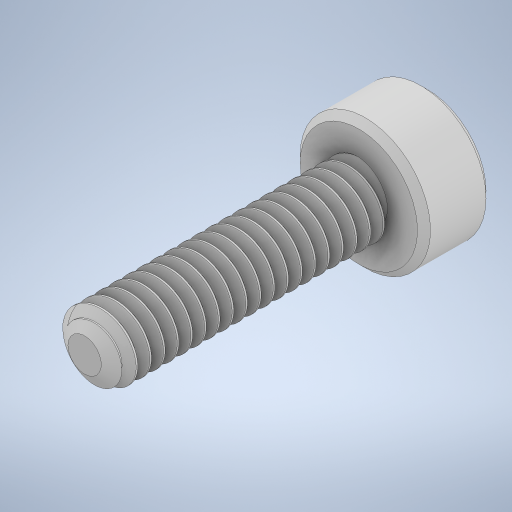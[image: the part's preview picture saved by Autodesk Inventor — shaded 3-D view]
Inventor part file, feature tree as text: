
AUTODESK INVENTOR PART (.ipt)
format: ipt  version: 2024 (Build 280153000, 153)  size: 845,824 bytes
history: native  units: mm
features: other x1, chamfer x1
ambient origin geometry x8: Origin, YZ Plane, XZ Plane, XY Plane, X Axis, Y Axis, Z Axis, Center Point
bodies: Body1 (feature_tree)
feature tree (2):
  other  "Těleso1"
  chamfer  "Chamfer1"  [1 undecoded]
note: 1 required parameter value undecoded (feature->parameter linkage not recoverable at this tier; creation-order binding heuristic only, values carry confidence <= 0.55)
